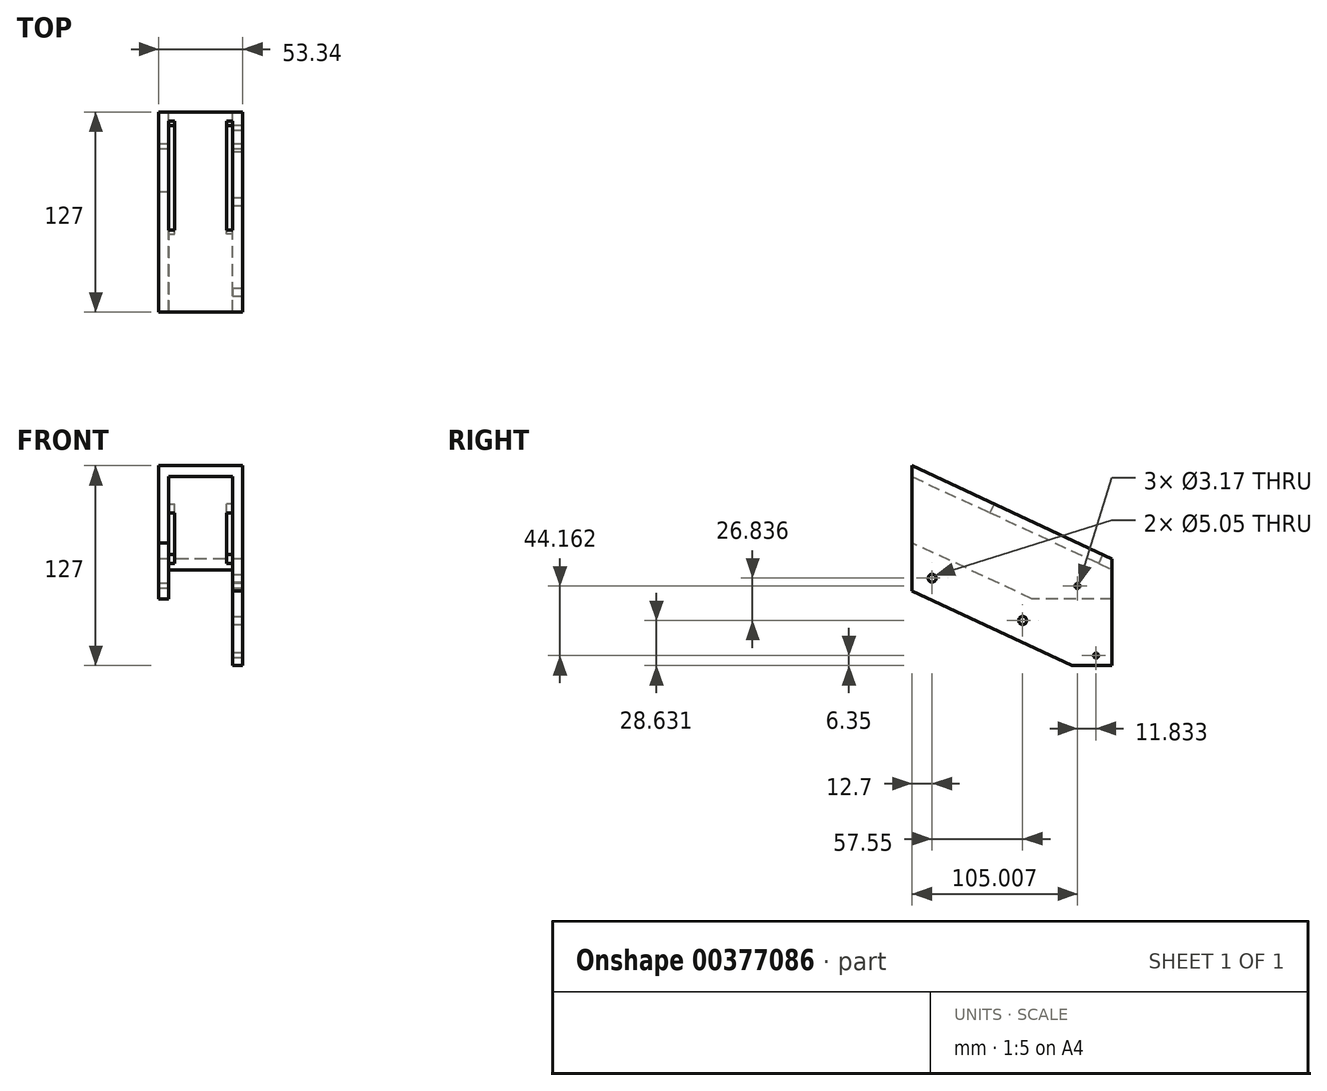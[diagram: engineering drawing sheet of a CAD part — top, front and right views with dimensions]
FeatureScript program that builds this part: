
annotation { "Feature Type Name" : "Feature", "Feature Type Description" : "" }
export const myFeature = defineFeature(function(context is Context, id is Id, definition is map)
    precondition{}
    {
        {
            var Q0;
            Q0=qCreatedBy(makeId("Right.planeOp"),FACE);
            var sketch = newSketch(context, id + "F0", { "sketchPlane" : qUnion([Q0])});
            skLineSegment(sketch, "E0.bottom", {"start": v(63.5, 4.28) * mm, "end": v(-63.5, 63.5) * mm});
            skLineSegment(sketch, "E0.top", {"start": v(63.5, -63.5) * mm, "end": v(-63.5, -63.5) * mm, "construction": true});
            skLineSegment(sketch, "E0.left", {"start": v(63.5, 4.28) * mm, "end": v(63.5, -63.5) * mm});
            skLineSegment(sketch, "E0.right", {"start": v(-63.5, 63.5) * mm, "end": v(-63.5, -63.5) * mm, "construction": true});
            skPoint(sketch, "E0.middle", {"position": v(0, 0) * mm});
            skLineSegment(sketch, "E1", {"start": v(41.5, -12.99) * mm, "end": v(53.34, -57.15) * mm, "construction": true});
            skCircle(sketch, "E2", {"center": v(41.5, -12.99) * mm, "radius": 1.59 * mm});
            skCircle(sketch, "E3", {"center": v(53.34, -57.15) * mm, "radius": 1.59 * mm});
            skLineSegment(sketch, "E4", {"start": v(-63.5, 63.5) * mm, "end": v(-63.5, -16.12) * mm});
            skLineSegment(sketch, "E5", {"start": v(-63.5, -16.12) * mm, "end": v(38.1, -63.5) * mm});
            skLineSegment(sketch, "E6", {"start": v(38.1, -63.5) * mm, "end": v(63.5, -63.5) * mm});
            skSolve(sketch);
        }
        {
            var Q0;
            Q0 = qSketchRegion(id + "F0", true);
            extrude(context, id + "F1", {"entities" : qUnion([Q0]), "depth" : 6.35 * mm});
        }
        {
            var Q0;
            Q0=makeQuery(id+"F1.opExtrude","CAP_FACE",FACE,{"disambiguationData":[OSD([sQuery(id+"F0.wireOp",EDGE,"E0.bottom"),sQuery(id+"F0.wireOp",EDGE,"E0.left"),sQuery(id+"F0.wireOp",EDGE,"E2"),sQuery(id+"F0.wireOp",EDGE,"E3"),sQuery(id+"F0.wireOp",EDGE,"E4"),sQuery(id+"F0.wireOp",EDGE,"E5"),sQuery(id+"F0.wireOp",EDGE,"E6")])],"isStart":true});
            var sketch = newSketch(context, id + "F2", { "sketchPlane" : qUnion([Q0])});
            skLineSegment(sketch, "E7", {"start": v(63.5, 56.5) * mm, "end": v(11.7, 32.34) * mm});
            skLineSegment(sketch, "E8", {"start": v(11.7, 32.34) * mm, "end": v(9.02, 38.1) * mm});
            skLineSegment(sketch, "E9", {"start": v(11.7, 32.34) * mm, "end": v(-55.06, 1.2) * mm});
            skLineSegment(sketch, "E10", {"start": v(-55.06, 1.2) * mm, "end": v(-63.5, -2.73) * mm});
            skLineSegment(sketch, "E11", {"start": v(-55.06, 1.2) * mm, "end": v(-57.74, 6.96) * mm});
            skSolve(sketch);
        }
        {
            var Q0;
            Q0 = qSketchRegion(id + "F2", true);
            var Q1;
            {var subQ0=sQuery(id+"F2.wireOp",EDGE,"E7");Q1=makeQuery(id+"F2.imprint","IMPRINT",FACE,{"disambiguationData":[TD([[makeQuery(id+"F2.imprint","IMPRINT",EDGE,{"derivedFrom":subQ0}),-1.0]])]});}
            var Q2;
            {var subQ0=sQuery(id+"F2.wireOp",EDGE,"E10");Q2=makeQuery(id+"F2.imprint","IMPRINT",FACE,{"disambiguationData":[TD([[makeQuery(id+"F2.imprint","IMPRINT",EDGE,{"derivedFrom":subQ0}),-1.0]])]});}
            var Q3;
            {var subQ0=sQuery(id+"F2.wireOp",EDGE,"E8");Q3=makeQuery(id+"F2.imprint","IMPRINT",FACE,{"disambiguationData":[TD([[makeQuery(id+"F2.imprint","IMPRINT",EDGE,{"derivedFrom":subQ0}),1.0]])]});}
            extrude(context, id + "F3", {"entities" : qUnion([Q0, Q1, Q2, Q3]), "operationType" : NewBodyOperationType.ADD, "depth" : 47 * mm});
        }
        {
            var Q0;
            {var subQ0=sQuery(id+"F2.wireOp",EDGE,"E8");var subQ1=sQuery(id+"F0.wireOp",EDGE,"E0.bottom");Q0=makeQuery(id+"FdCQDafgkdNC6di_1.boolean.opBoolean","MERGE",FACE,{"derivedFrom":[makeQuery(id+"F3.opExtrude","CAP_FACE",FACE,{"disambiguationData":[OSD([subQ1,sQuery(id+"F0.wireOp",EDGE,"E4"),sQuery(id+"F2.wireOp",EDGE,"E7"),subQ0])],"isStart":false}),makeQuery(id+"F3.opExtrude","CAP_FACE",FACE,{"disambiguationData":[OSD([subQ1,sQuery(id+"F0.wireOp",EDGE,"E0.left"),sQuery(id+"F2.wireOp",EDGE,"E10"),sQuery(id+"F2.wireOp",EDGE,"E11")])],"isStart":false}),makeQuery(id+"FdCQDafgkdNC6di_1.opExtrude","SWEPT_FACE",FACE,{"disambiguationData":[OSD([subQ0])]})]});}
            var sketch = newSketch(context, id + "F4", { "sketchPlane" : qUnion([Q0])});
            skLineSegment(sketch, "E12", {"start": v(-63.5, 4.28) * mm, "end": v(-63.5, -21.12) * mm});
            skLineSegment(sketch, "E13", {"start": v(-63.5, -21.12) * mm, "end": v(-12.7, -21.12) * mm});
            skLineSegment(sketch, "E14", {"start": v(-12.7, -21.12) * mm, "end": v(63.5, 14.41) * mm});
            skLineSegment(sketch, "E15", {"start": v(-63.5, 4.28) * mm, "end": v(63.5, 63.5) * mm});
            skLineSegment(sketch, "E16", {"start": v(63.5, 63.5) * mm, "end": v(63.5, 14.41) * mm});
            skCircle(sketch, "E17.0", {"center": v(-41.5, -12.99) * mm, "radius": 1.59 * mm});
            skSolve(sketch);
        }
        {
            var Q0;
            Q0 = qSketchRegion(id + "F4", true);
            extrude(context, id + "F5", {"entities" : qUnion([Q0]), "operationType" : NewBodyOperationType.ADD, "oppositeDirection" : true, "depth" : 6.35 * mm});
        }
        {
            var Q0;
            {var subQ0=sQuery(id+"F0.wireOp",EDGE,"E0.bottom");Q0=makeQuery(id+"F3.boolean.opBoolean","MERGE",FACE,{"derivedFrom":[makeQuery(id+"F1.opExtrude","SWEPT_FACE",FACE,{"disambiguationData":[OSD([subQ0])]}),makeQuery(id+"F3.opExtrude","SWEPT_FACE",FACE,{"disambiguationData":[OSD([subQ0])]})]});}
            var sketch = newSketch(context, id + "F6", { "sketchPlane" : qUnion([Q0])});
            skLineSegment(sketch, "E18.bottom", {"start": v(0, 49.4) * mm, "end": v(-3.81, 49.4) * mm});
            skLineSegment(sketch, "E18.top", {"start": v(0, -26.8) * mm, "end": v(-3.8, -26.8) * mm});
            skLineSegment(sketch, "E18.left", {"start": v(0, 49.4) * mm, "end": v(0, -26.8) * mm});
            skLineSegment(sketch, "E18.right", {"start": v(-3.81, 49.4) * mm, "end": v(-3.81, -26.8) * mm});
            skLineSegment(sketch, "E19", {"start": v(-20.32, 55.74) * mm, "end": v(-20.32, -84.39) * mm, "construction": true});
            skLineSegment(sketch, "E20.MirrorCS", {"start": v(-40.64, 49.4) * mm, "end": v(-36.83, 49.4) * mm});
            skLineSegment(sketch, "E21.MirrorCS", {"start": v(-40.64, -26.8) * mm, "end": v(-36.83, -26.8) * mm});
            skLineSegment(sketch, "E22.MirrorCS", {"start": v(-36.83, 49.4) * mm, "end": v(-36.83, -26.8) * mm});
            skLineSegment(sketch, "E23.MirrorCS", {"start": v(-40.64, 49.4) * mm, "end": v(-40.64, -26.8) * mm});
            skSolve(sketch);
        }
        {
            var Q0;
            Q0 = qSketchRegion(id + "F6", true);
            extrude(context, id + "F7", {"entities" : qUnion([Q0]), "operationType" : NewBodyOperationType.REMOVE, "endBound" : BoundingType.UP_TO_NEXT, "oppositeDirection" : true, "depth" : 25.4 * mm});
        }
        {
            var Q0;
            Q0=makeQuery(id+"F1.opExtrude","CAP_FACE",FACE,{"disambiguationData":[OSD([sQuery(id+"F0.wireOp",EDGE,"E0.bottom"),sQuery(id+"F0.wireOp",EDGE,"E0.left"),sQuery(id+"F0.wireOp",EDGE,"E2"),sQuery(id+"F0.wireOp",EDGE,"E3"),sQuery(id+"F0.wireOp",EDGE,"E4"),sQuery(id+"F0.wireOp",EDGE,"E5"),sQuery(id+"F0.wireOp",EDGE,"E6")])],"isStart":false});
            var sketch = newSketch(context, id + "F8", { "sketchPlane" : qUnion([Q0])});
            skCircle(sketch, "E24", {"center": v(-50.8, -8.03) * mm, "radius": 2.53 * mm});
            skCircle(sketch, "E25", {"center": v(6.75, -34.87) * mm, "radius": 2.53 * mm});
            skLineSegment(sketch, "E26", {"start": v(-50.8, -8.03) * mm, "end": v(6.75, -34.87) * mm, "construction": true});
            skSolve(sketch);
        }
        {
            var Q0;
            Q0 = qSketchRegion(id + "F8", true);
            extrude(context, id + "F9", {"entities" : qUnion([Q0]), "operationType" : NewBodyOperationType.REMOVE, "endBound" : BoundingType.UP_TO_NEXT, "oppositeDirection" : true, "depth" : 25.4 * mm});
        }
    });
